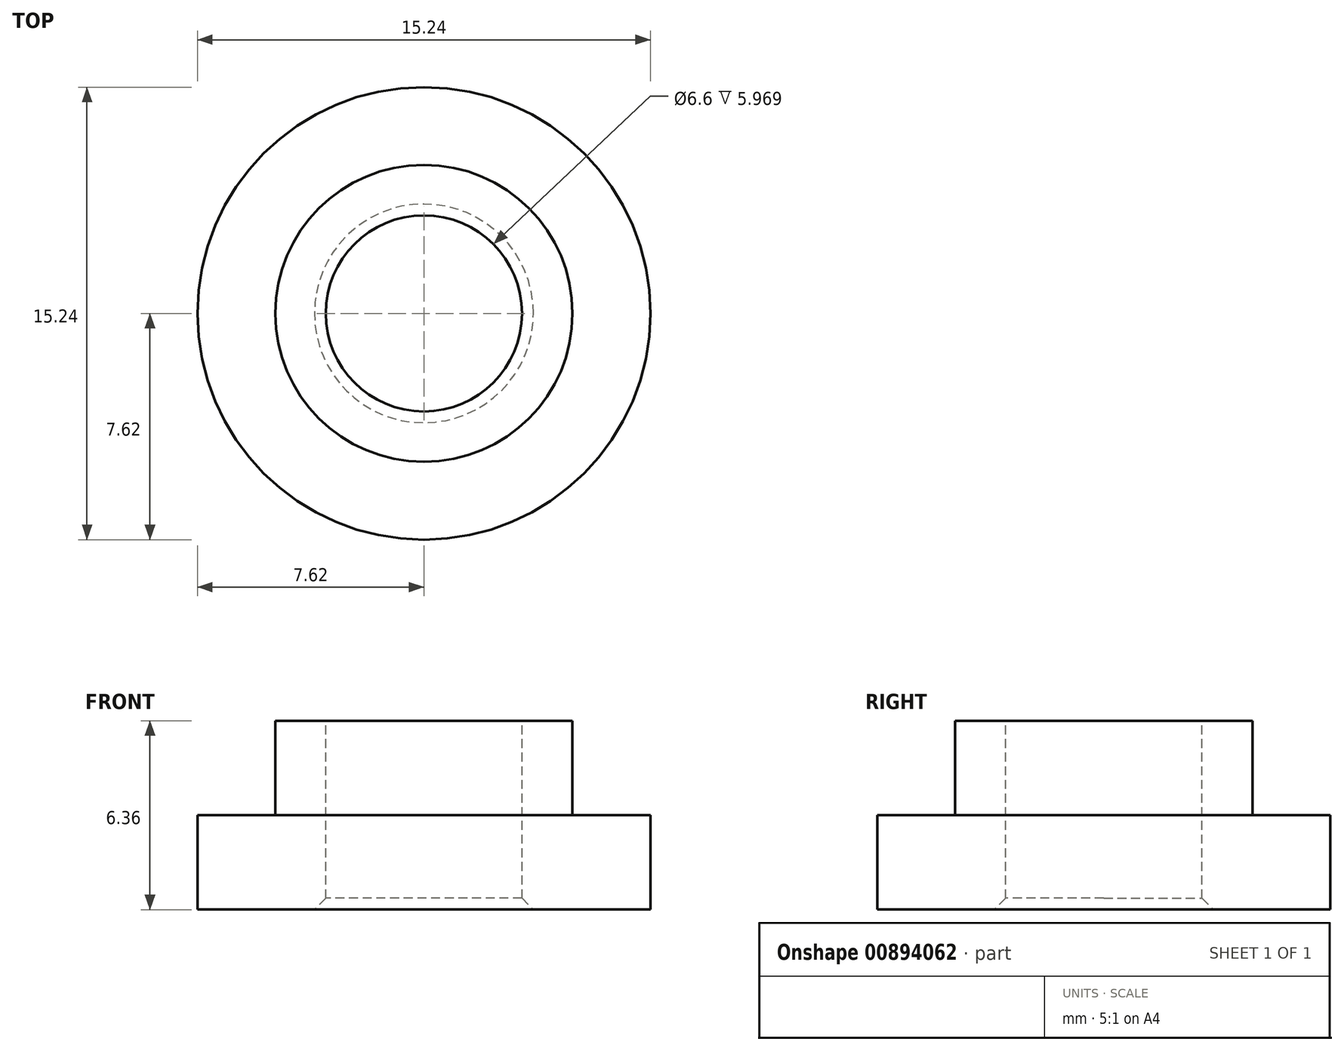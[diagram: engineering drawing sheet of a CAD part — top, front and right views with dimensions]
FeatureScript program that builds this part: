
annotation { "Feature Type Name" : "Feature", "Feature Type Description" : "" }
export const myFeature = defineFeature(function(context is Context, id is Id, definition is map)
    precondition{}
    {
        {
            var Q0;
            Q0=qCreatedBy(makeId("Top.planeOp"),FACE);
            var sketch = newSketch(context, id + "F0", { "sketchPlane" : qUnion([Q0])});
            skCircle(sketch, "E0", {"center": v(0, 0) * mm, "radius": 5 * mm});
            skSolve(sketch);
        }
        {
            var Q0;
            Q0=makeQuery(id+"F0.imprint","IMPRINT",FACE,{"disambiguationData":[TD([[makeQuery(id+"F0.imprint","IMPRINT",EDGE,{"derivedFrom":sQuery(id+"F0.wireOp",EDGE,"E0")}),1.0]])]});
            var Q1;
            Q1=sQuery(id+"F0.wireOp",EDGE,"E0");
            extrude(context, id + "F1", {"entities" : qUnion([Q0]), "surfaceEntities" : qUnion([Q1]), "depth" : 3.17 * mm, "offsetDistance" : 25.4 * mm});
        }
        {
            var Q0;
            Q0=makeQuery(id+"F1.opExtrude","CAP_FACE",FACE,{"disambiguationData":[OSD([sQuery(id+"F0.wireOp",EDGE,"E0")])],"isStart":true});
            var sketch = newSketch(context, id + "F2", { "sketchPlane" : qUnion([Q0])});
            skCircle(sketch, "E1", {"center": v(0, 0) * mm, "radius": 7.62 * mm});
            skSolve(sketch);
        }
        {
            var Q0;
            Q0=makeQuery(id+"F2.imprint","IMPRINT",FACE,{"disambiguationData":[TD([[makeQuery(id+"F2.imprint","IMPRINT",EDGE,{"derivedFrom":sQuery(id+"F2.wireOp",EDGE,"E1")}),1.0]])]});
            var Q1;
            Q1=makeQuery(id+"F2.imprint","IMPRINT",FACE,{"disambiguationData":[TD([[makeQuery(id+"F2.imprint","IMPRINT",EDGE,{"derivedFrom":makeQuery(id+"F1.opExtrude","CAP_EDGE",EDGE,{"disambiguationData":[OSD([sQuery(id+"F0.wireOp",EDGE,"E0")])],"isStart":true})}),-1.0]])]});
            extrude(context, id + "F3", {"entities" : qUnion([Q0, Q1]), "operationType" : NewBodyOperationType.ADD, "depth" : 3.17 * mm, "offsetDistance" : 25.4 * mm});
        }
        {
            var Q0;
            Q0=makeQuery(id+"F1.opExtrude","CAP_FACE",FACE,{"disambiguationData":[OSD([sQuery(id+"F0.wireOp",EDGE,"E0")])],"isStart":false});
            var sketch = newSketch(context, id + "F4", { "sketchPlane" : qUnion([Q0])});
            skCircle(sketch, "E2", {"center": v(0, 0) * mm, "radius": 3.3 * mm});
            skSolve(sketch);
        }
        {
            var Q0;
            Q0=makeQuery(id+"F4.imprint","IMPRINT",FACE,{"disambiguationData":[TD([[makeQuery(id+"F4.imprint","IMPRINT",EDGE,{"derivedFrom":sQuery(id+"F4.wireOp",EDGE,"E2")}),1.0]])]});
            extrude(context, id + "F5", {"entities" : qUnion([Q0]), "operationType" : NewBodyOperationType.REMOVE, "endBound" : BoundingType.THROUGH_ALL, "oppositeDirection" : true, "depth" : 25.4 * mm, "offsetDistance" : 25.4 * mm});
        }
        {
            var Q0;
            Q0=makeQuery(id+"F5.boolean.opBoolean","INTERSECT",EDGE,{"derivedFrom":[makeQuery(id+"F3.opExtrude","CAP_FACE",FACE,{"disambiguationData":[OSD([sQuery(id+"F2.wireOp",EDGE,"E1")])],"isStart":false}),makeQuery(id+"F5.opExtrude","SWEPT_FACE",FACE,{"disambiguationData":[OSD([sQuery(id+"F4.wireOp",EDGE,"E2")])]})]});
            chamfer(context, id + "F6", {"entities" : qUnion([Q0]), "width" : 0.38 * mm, "tangentPropagation" : true});
        }
    });
